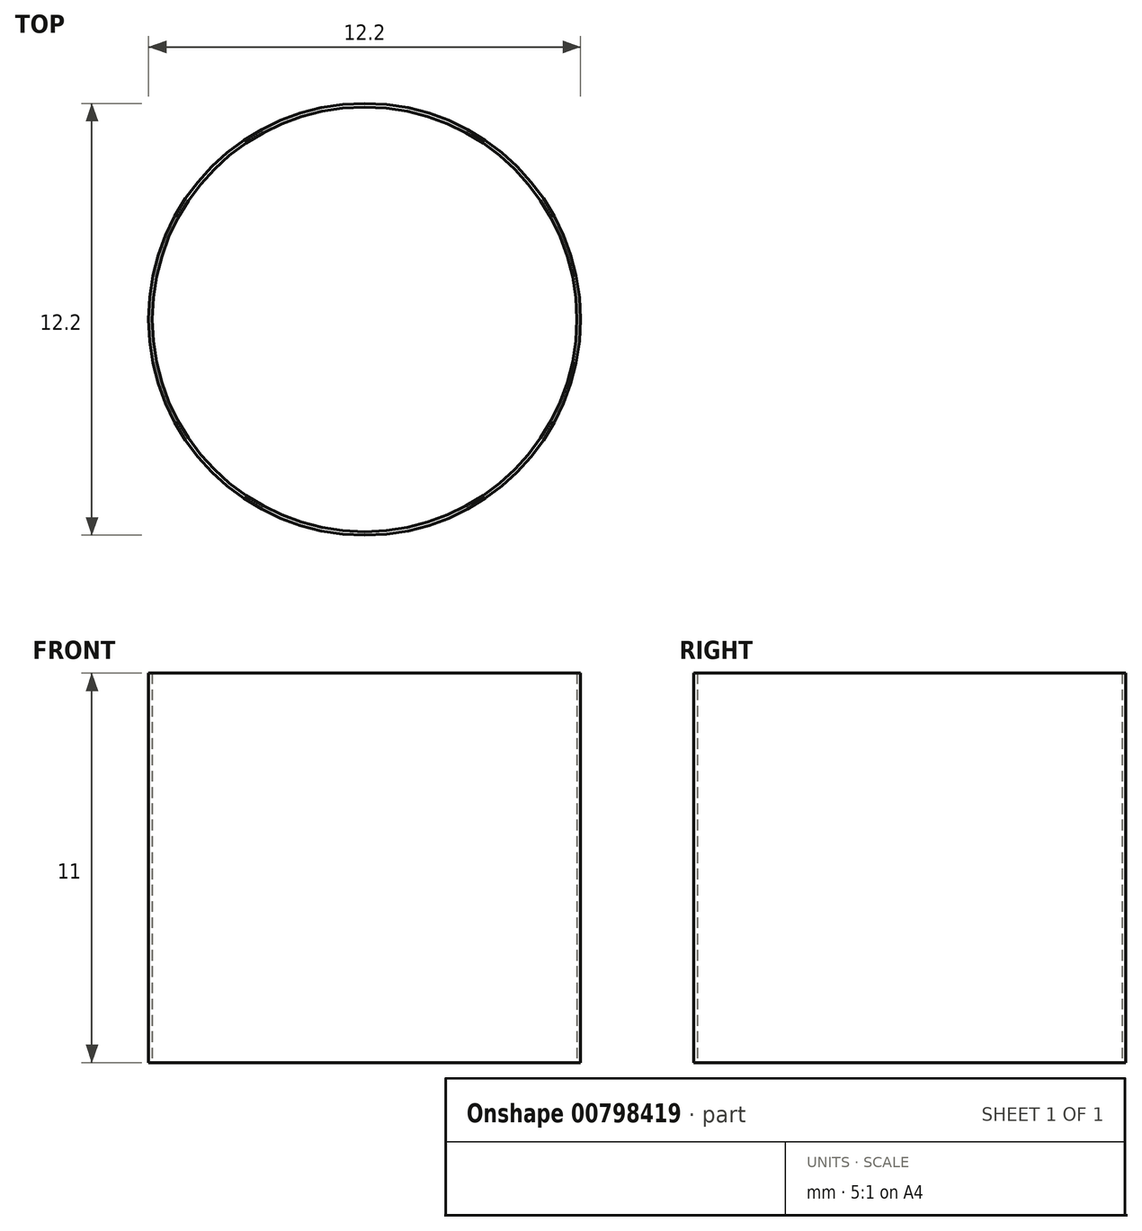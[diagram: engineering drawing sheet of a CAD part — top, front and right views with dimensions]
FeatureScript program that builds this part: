
annotation { "Feature Type Name" : "Feature", "Feature Type Description" : "" }
export const myFeature = defineFeature(function(context is Context, id is Id, definition is map)
    precondition{}
    {
        {
            var Q0;
            Q0=qCreatedBy(makeId("Top.planeOp"),FACE);
            var sketch = newSketch(context, id + "F0", { "sketchPlane" : qUnion([Q0])});
            skCircle(sketch, "E0", {"center": v(0, 0) * mm, "radius": 6 * mm});
            skCircle(sketch, "E1.0", {"center": v(0, 0) * mm, "radius": 6.1 * mm});
            skSolve(sketch);
        }
        {
            var Q0;
            Q0=makeQuery(id+"F0.imprint","IMPRINT",FACE,{"disambiguationData":[TD([[makeQuery(id+"F0.imprint","IMPRINT",EDGE,{"derivedFrom":sQuery(id+"F0.wireOp",EDGE,"E0")}),-1.0]])]});
            extrude(context, id + "F1", {"entities" : qUnion([Q0]), "depth" : 11 * mm, "offsetDistance" : 25 * mm});
        }
    });
